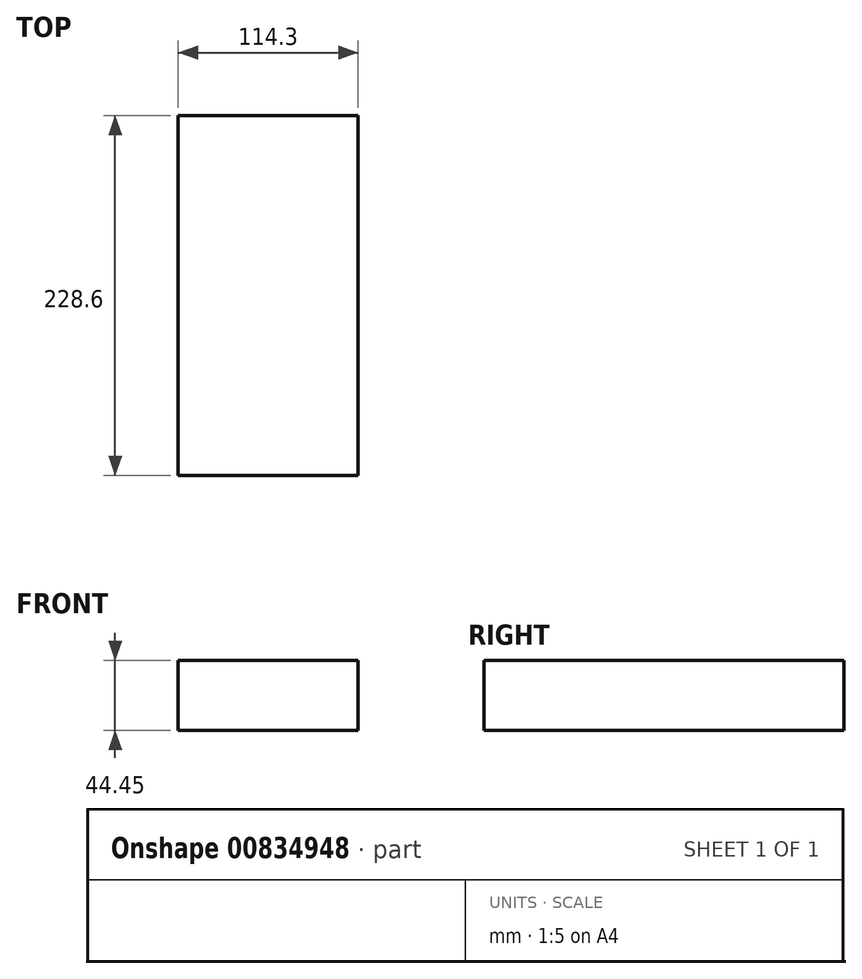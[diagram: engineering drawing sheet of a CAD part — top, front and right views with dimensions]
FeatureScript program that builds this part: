
annotation { "Feature Type Name" : "Feature", "Feature Type Description" : "" }
export const myFeature = defineFeature(function(context is Context, id is Id, definition is map)
    precondition{}
    {
        {
            var Q0;
            Q0=qCreatedBy(makeId("Front.planeOp"),FACE);
            var sketch = newSketch(context, id + "F0", { "sketchPlane" : qUnion([Q0])});
            skLineSegment(sketch, "E0.bottom", {"start": v(0, 0) * mm, "end": v(114.3, 0) * mm});
            skLineSegment(sketch, "E0.top", {"start": v(0, 44.45) * mm, "end": v(114.3, 44.45) * mm});
            skLineSegment(sketch, "E0.left", {"start": v(0, 0) * mm, "end": v(0, 44.45) * mm});
            skLineSegment(sketch, "E0.right", {"start": v(114.3, 0) * mm, "end": v(114.3, 44.45) * mm});
            skSolve(sketch);
        }
        {
            var Q0;
            Q0 = qSketchRegion(id + "F0", true);
            extrude(context, id + "F1", {"entities" : qUnion([Q0]), "depth" : 228.6 * mm, "offsetDistance" : 25.4 * mm});
        }
    });
